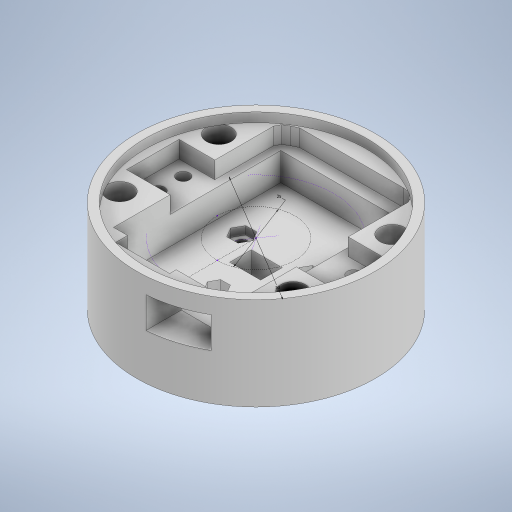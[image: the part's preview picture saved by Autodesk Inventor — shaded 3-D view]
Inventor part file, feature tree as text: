
AUTODESK INVENTOR PART (.ipt)
format: ipt  version: 2024 (Build 280153000, 153)  size: 690,688 bytes
history: native  units: mm
features: sketch x17, extrude x12, hole x1, pattern_circular x1
ambient origin geometry x8: Origin, YZ Plane, XZ Plane, XY Plane, X Axis, Y Axis, Z Axis, Center Point
bodies: Solid1 (feature_tree)
feature tree (31):
  extrude  "Extrusion1"  Depth=20.0mm TaperAngle=0.0deg
  sketch  "Sketch2"  dims[d3=50.0mm d64=25.0mm]
  sketch  "Sketch15"  dims[d70=3.5mm d71=6.0mm d72=4.0mm d73=2.0mm d74=90.0deg d75=8.0mm d76=20.594885mm d77=30.0mm d78=360.0deg]
  hole  "Hole2"  [1 undecoded]
  pattern_circular  "Circular Pattern4"  Count=3 Angle=360.0deg
  extrude  "Extrusion13"  Depth=10.0mm TaperAngle=0.0deg
  extrude  "Extrusion14"  Depth=3.0mm TaperAngle=0.0deg
  extrude  "Extrusion15"  Depth=16.0mm
  extrude  "Extrusion17"  Depth=15.0mm TaperAngle=0.0deg
  sketch  "Sketch32"  dims[d95=38.0mm d96=54.0mm]
  extrude  "Extrusion19"  Depth=54.0mm
  extrude  "Extrusion20"  Depth=4.0mm
  extrude  "Extrusion21"  Depth=11.2mm
  sketch  "Sketch42"  dims[d119=5.4mm d120=3.5mm d121=0.0mm]
  extrude  "Extrusion22"  Depth=0.5mm
  extrude  "Extrusion23"  Depth=3.5mm TaperAngle=0.0deg
  extrude  "Extrusion25"  Depth=2.6mm TaperAngle=0.0deg
  sketch  "Sketch46"  dims[d133=7.0mm]
  extrude  "Extrusion26"  Depth=3.5mm TaperAngle=0.0deg
  sketch  "Sketch1"  dims[d0=77.0mm d1=20.0mm d2=0.0mm]
  sketch  "Sketch27"  dims[d81=77.0mm d82=10.0mm d83=0.0mm]
  sketch  "Sketch28"  dims[d84=71.5mm d85=3.0mm d86=0.0mm]
  sketch  "Sketch29"  dims[d87=28.0mm d88=16.0mm]
  sketch  "Sketch31"  dims[d89=8.0mm d90=15.0mm d91=0.0mm]
  sketch  "Sketch34"  dims[d97=14.5mm d98=0.0mm d105=4.0mm]
  sketch  "Sketch36"  dims[d106=11.2mm d107=0.0mm d108=55.0mm]
  sketch  "Sketch41"  dims[d114=5.5mm d115=0.0mm d117=0.5mm]
  sketch  "Sketch43"  dims[d122=5.4mm d123=2.6mm d124=0.0mm]
  sketch  "Sketch44"  dims[d125=5.4mm d126=3.5mm d127=0.0mm]
  sketch  "Sketch45"  dims[d132=10.0mm]
  sketch  "Sketch47"  dims[d134=0.0mm d135=0.0mm d139=16.1mm d140=10.0mm d141=0.0mm d142=0.0mm d143=4.0mm d12=0.5mm d13=0.872665mm d14=0.5mm d15=0.872665mm d17=0.5mm d18=0.872665mm d19=0.5mm d20=0.872665mm d28=1.0mm d29=1.0mm d30=1.0mm d31=0.15mm d32=0.25mm d33=0.375mm d34=14.3117mm d35=0.75mm d36=20.594885mm d37=0.0625mm d38=0.75mm d39=0.375mm d42=0.5mm d43=0.872665mm d44=0.5mm d45=0.872665mm d144=0.5mm d145=0.872665mm d146=0.5mm d147=0.872665mm]
note: 1 required parameter value undecoded (feature->parameter linkage not recoverable at this tier; creation-order binding heuristic only, values carry confidence <= 0.55)
